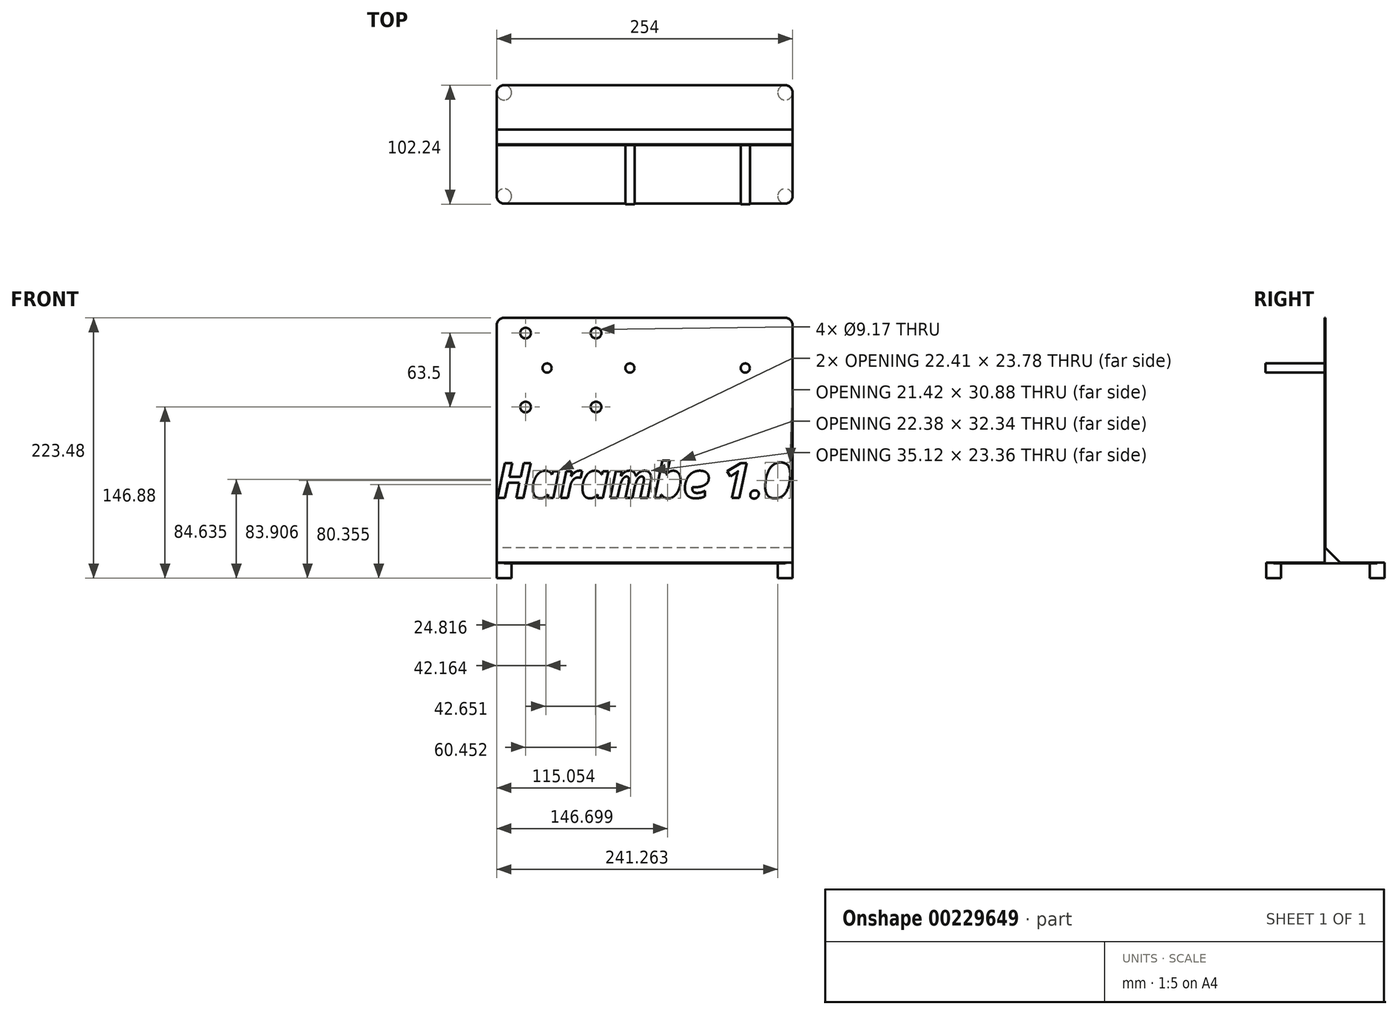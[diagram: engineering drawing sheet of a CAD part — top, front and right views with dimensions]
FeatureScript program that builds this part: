
annotation { "Feature Type Name" : "Feature", "Feature Type Description" : "" }
export const myFeature = defineFeature(function(context is Context, id is Id, definition is map)
    precondition{}
    {
        {
            var Q0;
            Q0=qCreatedBy(makeId("Front.planeOp"),FACE);
            var sketch = newSketch(context, id + "F0", { "sketchPlane" : qUnion([Q0])});
            skLineSegment(sketch, "E0.top", {"start": v(6.35, 254) * mm, "end": v(247.65, 254) * mm});
            skLineSegment(sketch, "E0.left", {"start": v(0, 6.35) * mm, "end": v(0, 76.6) * mm});
            skLineSegment(sketch, "E0.right", {"start": v(254, 6.35) * mm, "end": v(254, 76.6) * mm});
            skPoint(sketch, "E1.visualSharp", {"position": v(0, 254) * mm});
            skArc(sketch, "E1.filletArc", {"start": v(6.35, 254) * mm, "mid": v(1.86, 252.14) * mm, "end": v(0, 247.65) * mm});
            skPoint(sketch, "E2.visualSharp", {"position": v(254, 254) * mm});
            skArc(sketch, "E2.filletArc", {"start": v(254, 247.65) * mm, "mid": v(252.14, 252.14) * mm, "end": v(247.65, 254) * mm});
            skPoint(sketch, "E3.visualSharp", {"position": v(254, 0) * mm});
            skPoint(sketch, "E4.visualSharp", {"position": v(0, 0) * mm});
            skLineSegment(sketch, "E5", {"start": v(20.12, 0) * mm, "end": v(20.12, 76.2) * mm, "construction": true});
            skLineSegment(sketch, "E6", {"start": v(20.12, 76.2) * mm, "end": v(89.97, 76.2) * mm, "construction": true});
            skLineSegment(sketch, "E7", {"start": v(89.97, 76.2) * mm, "end": v(89.97, 0) * mm, "construction": true});
            skLineSegment(sketch, "E8", {"start": v(55.04, 99.97) * mm, "end": v(55.04, -7.84) * mm, "construction": true});
            skPoint(sketch, "E9", {"position": v(24.82, 69.85) * mm});
            skPoint(sketch, "E10", {"position": v(43.23, 39.88) * mm});
            skLineSegment(sketch, "E11", {"start": v(8, 38.1) * mm, "end": v(115.16, 38.1) * mm, "construction": true});
            skPoint(sketch, "E12.MirrorP", {"position": v(85.27, 69.85) * mm});
            skPoint(sketch, "E13.MirrorP", {"position": v(24.82, 6.35) * mm});
            skPoint(sketch, "E14.MirrorP", {"position": v(85.27, 6.35) * mm});
            skCircle(sketch, "E15", {"center": v(43.23, 39.88) * mm, "radius": 3.94 * mm});
            skLineSegment(sketch, "E16", {"start": v(6.35, 82.95) * mm, "end": v(247.65, 82.95) * mm});
            skPoint(sketch, "E17.visualSharp", {"position": v(0, 82.95) * mm});
            skArc(sketch, "E17.filletArc", {"start": v(6.35, 82.95) * mm, "mid": v(1.86, 81.09) * mm, "end": v(0, 76.6) * mm});
            skPoint(sketch, "E18.visualSharp", {"position": v(254, 82.95) * mm});
            skArc(sketch, "E18.filletArc", {"start": v(254, 76.6) * mm, "mid": v(252.14, 81.09) * mm, "end": v(247.65, 82.95) * mm});
            skLineSegment(sketch, "E19", {"start": v(0, 6.35) * mm, "end": v(0, -120.84) * mm});
            skLineSegment(sketch, "E20", {"start": v(6.35, -127.2) * mm, "end": v(247.65, -127.2) * mm});
            skLineSegment(sketch, "E21", {"start": v(254, -120.84) * mm, "end": v(254, 6.35) * mm});
            skText(sketch, "E22", { "text": "Harambe 1.0", "fontName": "OpenSans-BoldItalic.ttf"});
            skPoint(sketch, "E23.visualSharp", {"position": v(254, -127.2) * mm});
            skLineSegment(sketch, "E24", {"start": v(0, -120.84) * mm, "end": v(0, -127.2) * mm});
            skLineSegment(sketch, "E25", {"start": v(0, -127.2) * mm, "end": v(6.35, -127.2) * mm});
            skLineSegment(sketch, "E26", {"start": v(254, -120.84) * mm, "end": v(254, -127.2) * mm});
            skLineSegment(sketch, "E27", {"start": v(247.65, -127.2) * mm, "end": v(254, -127.2) * mm});
            const initialGuessF0  = {"E22": [-0.0003, -0.07165, 1, 0, 0.03025]};
            skSetInitialGuess(sketch, initialGuessF0);
            skSolve(sketch);
        }
        {
            var Q0;
            Q0=makeQuery(id+"F0.imprint","IMPRINT",FACE,{"disambiguationData":[TD([[makeQuery(id+"F0.imprint","IMPRINT",EDGE,{"derivedFrom":sQuery(id+"F0.wireOp",EDGE,"E0.bottom")}),1.0]])]});
            var Q1;
            Q1=makeQuery(id+"F0.imprint","IMPRINT",FACE,{"disambiguationData":[TD([[makeQuery(id+"F0.imprint","IMPRINT",EDGE,{"derivedFrom":sQuery(id+"F0.wireOp",EDGE,"E0.left")}),-1.0]])]});
            extrude(context, id + "F1", {"entities" : qUnion([Q0, Q1]), "depth" : 0.64 * mm});
        }
        {
            var Q0;
            Q0=sQuery(id+"F0.wireOp",VERTEX,"E9");
            var Q1;
            Q1=sQuery(id+"F0.wireOp",VERTEX,"E12.MirrorP");
            var Q2;
            Q2=sQuery(id+"F0.wireOp",VERTEX,"E14.MirrorP");
            var Q3;
            Q3=sQuery(id+"F0.wireOp",VERTEX,"E13.MirrorP");
            var Q4;
            Q4=makeQuery(id+"F1.opExtrude","SWEPT_BODY",BODY,{"disambiguationData":[OSD([sQuery(id+"F0.wireOp",EDGE,"E0.bottom"),sQuery(id+"F0.wireOp",EDGE,"E0.top"),sQuery(id+"F0.wireOp",EDGE,"E0.left"),sQuery(id+"F0.wireOp",EDGE,"E0.right"),sQuery(id+"F0.wireOp",EDGE,"E1.filletArc"),sQuery(id+"F0.wireOp",EDGE,"E2.filletArc"),sQuery(id+"F0.wireOp",EDGE,"E3.filletArc"),sQuery(id+"F0.wireOp",EDGE,"E4.filletArc"),sQuery(id+"F0.wireOp",EDGE,"E15")])]});
            hole(context, id + "F2", {"style" : HoleStyle.SIMPLE, "endStyle" : HoleEndStyle.THROUGH, "oppositeDirection" : true, "holeDiameter" : 9.17 * mm, "locations" : qUnion([Q0, Q1, Q2, Q3]), "scope" : qUnion([Q4]), "isTappedThrough" : true});
        }
        {
            var Q0;
            Q0=makeQuery(id+"F1.opExtrude","CAP_FACE",FACE,{"disambiguationData":[OSD([sQuery(id+"F0.wireOp",EDGE,"E0.bottom"),sQuery(id+"F0.wireOp",EDGE,"E0.top"),sQuery(id+"F0.wireOp",EDGE,"E0.left"),sQuery(id+"F0.wireOp",EDGE,"E0.right"),sQuery(id+"F0.wireOp",EDGE,"E1.filletArc"),sQuery(id+"F0.wireOp",EDGE,"E2.filletArc"),sQuery(id+"F0.wireOp",EDGE,"E3.filletArc"),sQuery(id+"F0.wireOp",EDGE,"E4.filletArc"),sQuery(id+"F0.wireOp",EDGE,"E15")])],"isStart":false});
            var sketch = newSketch(context, id + "F3", { "sketchPlane" : qUnion([Q0])});
            skPoint(sketch, "E28", {"position": v(43.23, 39.88) * mm});
            skCircle(sketch, "E29", {"center": v(114.35, 39.88) * mm, "radius": 3.94 * mm});
            skCircle(sketch, "E30", {"center": v(213.41, 39.88) * mm, "radius": 3.94 * mm});
            skSolve(sketch);
        }
        {
            var Q0;
            Q0 = qSketchRegion(id + "F3", true);
            extrude(context, id + "F4", {"entities" : qUnion([Q0]), "operationType" : NewBodyOperationType.ADD, "depth" : 50.8 * mm});
        }
        {
            var Q0;
            Q0=makeQuery(id+"F1.opExtrude","SWEPT_FACE",FACE,{"disambiguationData":[OSD([sQuery(id+"F0.wireOp",EDGE,"E20")])]});
            var sketch = newSketch(context, id + "F5", { "sketchPlane" : qUnion([Q0])});
            skLineSegment(sketch, "E31", {"start": v(0, -44.45) * mm, "end": v(0, 44.45) * mm});
            skLineSegment(sketch, "E32", {"start": v(6.35, 50.8) * mm, "end": v(247.65, 50.8) * mm});
            skLineSegment(sketch, "E33", {"start": v(254, 44.45) * mm, "end": v(254, -44.45) * mm});
            skLineSegment(sketch, "E34", {"start": v(247.65, -50.8) * mm, "end": v(6.35, -50.8) * mm});
            skPoint(sketch, "E35.visualSharp", {"position": v(0, 50.8) * mm});
            skArc(sketch, "E35.filletArc", {"start": v(6.35, 50.8) * mm, "mid": v(1.86, 48.94) * mm, "end": v(0, 44.45) * mm});
            skPoint(sketch, "E36.visualSharp", {"position": v(254, 50.8) * mm});
            skArc(sketch, "E36.filletArc", {"start": v(254, 44.45) * mm, "mid": v(252.14, 48.94) * mm, "end": v(247.65, 50.8) * mm});
            skPoint(sketch, "E37.visualSharp", {"position": v(254, -50.8) * mm});
            skArc(sketch, "E37.filletArc", {"start": v(247.65, -50.8) * mm, "mid": v(252.14, -48.94) * mm, "end": v(254, -44.45) * mm});
            skPoint(sketch, "E38.visualSharp", {"position": v(0, -50.8) * mm});
            skArc(sketch, "E38.filletArc", {"start": v(0, -44.45) * mm, "mid": v(1.86, -48.94) * mm, "end": v(6.35, -50.8) * mm});
            skSolve(sketch);
        }
        {
            var Q0;
            Q0 = qSketchRegion(id + "F5", true);
            extrude(context, id + "F6", {"entities" : qUnion([Q0]), "operationType" : NewBodyOperationType.ADD, "depth" : 0.64 * mm});
        }
        {
            var Q0;
            Q0=makeQuery(id+"F6.opExtrude","CAP_FACE",FACE,{"disambiguationData":[OSD([sQuery(id+"F5.wireOp",EDGE,"E31"),sQuery(id+"F5.wireOp",EDGE,"E32"),sQuery(id+"F5.wireOp",EDGE,"E33"),sQuery(id+"F5.wireOp",EDGE,"E34"),sQuery(id+"F5.wireOp",EDGE,"E35.filletArc"),sQuery(id+"F5.wireOp",EDGE,"E36.filletArc"),sQuery(id+"F5.wireOp",EDGE,"E37.filletArc"),sQuery(id+"F5.wireOp",EDGE,"E38.filletArc")])],"isStart":false});
            var sketch = newSketch(context, id + "F7", { "sketchPlane" : qUnion([Q0])});
            skCircle(sketch, "E39", {"center": v(6.35, 44.45) * mm, "radius": 6.35 * mm});
            skCircle(sketch, "E40", {"center": v(247.65, 44.45) * mm, "radius": 6.35 * mm});
            skCircle(sketch, "E41", {"center": v(247.65, -44.45) * mm, "radius": 6.35 * mm});
            skCircle(sketch, "E42", {"center": v(6.35, -44.45) * mm, "radius": 6.35 * mm});
            skSolve(sketch);
        }
        {
            var Q0;
            {var subQ0=sQuery(id+"F7.wireOp",EDGE,"E40");var subQ1=makeQuery(id+"F7.imprint","INTERSECT",VERTEX,{"derivedFrom":[makeQuery(id+"F6.opExtrude","CAP_EDGE",EDGE,{"disambiguationData":[OSD([sQuery(id+"F5.wireOp",EDGE,"E32")])],"isStart":false}),subQ0]});Q0=makeQuery(id+"F7.imprint","IMPRINT",FACE,{"disambiguationData":[TD([[makeQuery(id+"F7.imprint","IMPRINT",EDGE,{"disambiguationData":[TD([[subQ1,1.0]])],"derivedFrom":subQ0}),1.0]])]});}
            var Q1;
            {var subQ0=sQuery(id+"F7.wireOp",EDGE,"E41");var subQ1=makeQuery(id+"F7.imprint","INTERSECT",VERTEX,{"derivedFrom":[makeQuery(id+"F6.opExtrude","CAP_EDGE",EDGE,{"disambiguationData":[OSD([sQuery(id+"F5.wireOp",EDGE,"E34")])],"isStart":false}),subQ0]});Q1=makeQuery(id+"F7.imprint","IMPRINT",FACE,{"disambiguationData":[TD([[makeQuery(id+"F7.imprint","IMPRINT",EDGE,{"disambiguationData":[TD([[subQ1,1.0]])],"derivedFrom":subQ0}),1.0]])]});}
            var Q2;
            {var subQ0=sQuery(id+"F7.wireOp",EDGE,"E42");var subQ1=makeQuery(id+"F7.imprint","INTERSECT",VERTEX,{"derivedFrom":[makeQuery(id+"F6.opExtrude","CAP_EDGE",EDGE,{"disambiguationData":[OSD([sQuery(id+"F5.wireOp",EDGE,"E31")])],"isStart":false}),subQ0]});Q2=makeQuery(id+"F7.imprint","IMPRINT",FACE,{"disambiguationData":[TD([[makeQuery(id+"F7.imprint","IMPRINT",EDGE,{"disambiguationData":[TD([[subQ1,-1.0]])],"derivedFrom":subQ0}),1.0]])]});}
            var Q3;
            {var subQ0=sQuery(id+"F7.wireOp",EDGE,"E39");var subQ1=makeQuery(id+"F7.imprint","INTERSECT",VERTEX,{"derivedFrom":[makeQuery(id+"F6.opExtrude","CAP_EDGE",EDGE,{"disambiguationData":[OSD([sQuery(id+"F5.wireOp",EDGE,"E32")])],"isStart":false}),subQ0]});Q3=makeQuery(id+"F7.imprint","IMPRINT",FACE,{"disambiguationData":[TD([[makeQuery(id+"F7.imprint","IMPRINT",EDGE,{"disambiguationData":[TD([[subQ1,-1.0]])],"derivedFrom":subQ0}),1.0]])]});}
            extrude(context, id + "F8", {"entities" : qUnion([Q0, Q1, Q2, Q3]), "operationType" : NewBodyOperationType.ADD, "depth" : 12.7 * mm});
        }
        {
            var Q0;
            Q0=makeQuery(id+"F1.opExtrude","CAP_EDGE",EDGE,{"disambiguationData":[OSD([sQuery(id+"F0.wireOp",EDGE,"E20"),sQuery(id+"F0.wireOp",EDGE,"E25"),sQuery(id+"F0.wireOp",EDGE,"E27")])],"isStart":false});
            var Q1;
            Q1=makeQuery(id+"F1.opExtrude","CAP_EDGE",EDGE,{"disambiguationData":[OSD([sQuery(id+"F0.wireOp",EDGE,"E20"),sQuery(id+"F0.wireOp",EDGE,"E25"),sQuery(id+"F0.wireOp",EDGE,"E27")])],"isStart":true});
            chamfer(context, id + "F9", {"entities" : qUnion([Q0, Q1]), "width" : 12.7 * mm, "tangentPropagation" : true});
        }
    });
